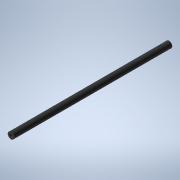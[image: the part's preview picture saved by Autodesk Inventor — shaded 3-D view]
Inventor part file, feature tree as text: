
AUTODESK INVENTOR PART (.ipt)
format: ipt  version: 2021 (Build 250183000, 183)  size: 94,208 bytes
history: native  units: mm
features: extrude x1, sketch x1
ambient origin geometry x8: Origin, YZ Plane, XZ Plane, XY Plane, X Axis, Y Axis, Z Axis, Center Point
bodies: Solid1 (feature_tree)
feature tree (2):
  extrude  "Extrusion1"  Depth=4.0mm
  sketch  "Sketch1"  dims[d0=8.0mm d1=4.0mm d2=200.0mm d3=0.0mm]
